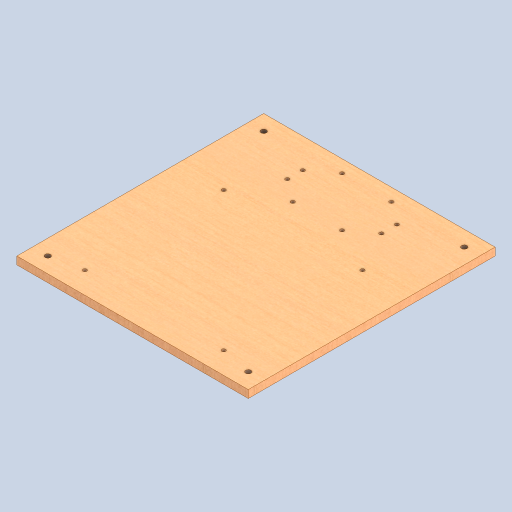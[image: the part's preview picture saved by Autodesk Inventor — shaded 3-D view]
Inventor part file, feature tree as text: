
AUTODESK INVENTOR PART (.ipt)
format: ipt  version: 2023 (Build 270158000, 158)  size: 241,152 bytes
history: native  units: mm
features: sketch x3, hole x2, other x1, extrude x1
ambient origin geometry x8: Origin, YZ Plane, XZ Plane, XY Plane, X Axis, Y Axis, Z Axis, Center Point
bodies: Body1 (feature_tree)
feature tree (7):
  other  "Sólido1"
  extrude  "Extrusão1"  Depth=320.0mm
  hole  "Hole1"  [1 undecoded]
  hole  "Hole2"  [1 undecoded]
  sketch  "Esboço1"  dims[d0=300.0mm d1=320.0mm]
  sketch  "Sketch2"  dims[d2=10.0mm d3=0.0mm]
  sketch  "Sketch3"  dims[d5=20.0mm d7=20.0mm d9=20.0mm d11=20.0mm d13=20.0mm d15=20.0mm d16=64.0mm d17=64.0mm d18=300.0mm d19=320.0mm d20=16.4mm d21=118.0mm d22=122.0mm d23=20.0mm d24=38.4mm d25=89.0mm d26=180.0mm d27=180.0mm d28=60.0mm d29=28.1mm d30=5.0mm d31=6.0mm d32=4.0mm d33=2.0mm d34=90.0deg d35=0.5mm d36=20.594885mm d38=20.0mm d40=20.0mm d41=280.0mm d42=260.0mm d43=320.0mm d44=300.0mm d45=20.0mm d46=20.0mm d47=7.133974mm d48=16.0mm d49=4.0mm d50=2.0mm d51=90.0deg d52=8.0mm d53=20.594885mm]
note: 2 required parameter values undecoded (feature->parameter linkage not recoverable at this tier; creation-order binding heuristic only, values carry confidence <= 0.55)
